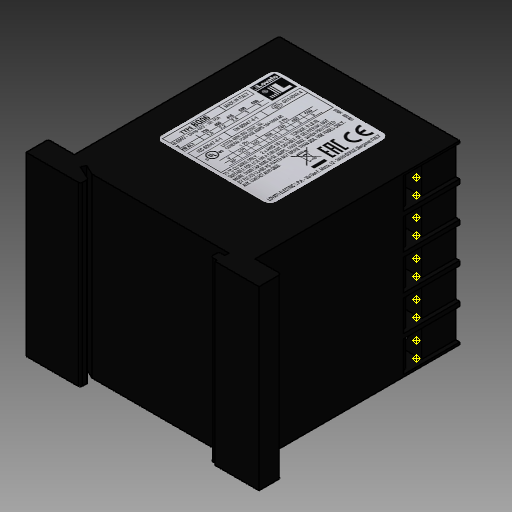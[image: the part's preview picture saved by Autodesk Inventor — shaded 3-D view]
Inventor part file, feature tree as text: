
AUTODESK INVENTOR PART (.ipt)
format: ipt  version: 2025.2 (Build 292293000, 293)  size: 1,169,408 bytes
history: native  units: mm
features: other x25, sketch x9, projected_geometry x9, extrude x7, fillet x1, mirror x1
ambient origin geometry x8: Origin, YZ Plane, XZ Plane, XY Plane, X Axis, Y Axis, Z Axis, Center Point
bodies: Solid1 (feature_tree)
feature tree (52):
  extrude  "Extrusion1"  Depth=6.5mm
  extrude  "Extrusion9"  Depth=5.5mm
  fillet  "Fillet2"  Radius=3.5mm
  extrude  "Extrusion10"  Depth=13.5mm
  extrude  "Extrusion11"  Depth=1.2mm
  extrude  "Extrusion13"  Depth=12.5mm
  extrude  "Extrusion14"  Depth=1.0mm
  other  "Decal1"
  other  "Decal2"
  other  "Sredina"
  sketch  "Sketch17"  dims[d18=44.0mm d19=0.0mm d20=0.5mm d21=55.5mm d93=6.0mm d99=40.0mm d101=8.5mm d102=10.0mm d104=10.0mm d107=8.0mm d108=5.0mm d109=6.0mm d110=5.0mm d111=7.0mm d112=9.0mm d113=3.0mm d114=7.5mm d115=1.0mm d116=0.0mm d117=0.5mm d118=14.0mm d119=7.7mm d120=0.95mm d121=50.0mm d123=8.6mm d124=10.0mm d126=10.0mm d128=0.95mm d129=1.0mm d130=0.0mm d131=4.0mm d132=8.5mm d133=50.0mm d135=8.6mm d136=10.0mm d138=10.0mm d140=10.0mm d141=0.0mm d142=10.0mm d143=8.8mm d145=10.0mm d147=50.0mm d148=1.05mm d149=14.0mm d150=7.7mm d152=0.0mm d153=1.0mm d154=4.0mm d155=8.5mm d156=50.0mm d158=8.8mm d159=10.0mm d161=10.0mm d163=10.0mm d164=0.0mm d165=10.0mm d166=0.0mm d172=44.0mm d173=45.0mm d186=30.0mm d199=3.85mm d200=7.7mm d201=3.0mm]
  other  "Work Point1"
  other  "Work Point2"
  other  "Work Point3"
  other  "Work Point4"
  other  "Work Point5"
  other  "Work Point6"
  other  "Work Point7"
  other  "Work Point8"
  other  "Work Point9"
  other  "Work Point10"
  mirror  "Mirror1"
  sketch  "Sketch9"  dims[d13=11.0mm d14=1.0mm]
  sketch  "Sketch Rectangular Pattern1"  dims[d0=58.0mm d1=6.5mm]
  sketch  "Sketch Rectangular Pattern2"  dims[d2=6.5mm d4=5.5mm d6=3.5mm]
  projected_geometry  "Projected Loop9"
  projected_geometry  "Projected Loop10"
  projected_geometry  "Projected Loop11"
  projected_geometry  "Projected Loop12"
  sketch  "Sketch Rectangular Pattern3"  dims[d7=13.5mm d8=1.9mm]
  sketch  "Sketch12"  dims[d15=0.5mm d16=3.5mm]
  sketch  "Sketch Rectangular Pattern4"  dims[d9=1.2mm d10=4.363323mm]
  projected_geometry  "Projected Loop13"
  projected_geometry  "Projected Loop14"
  projected_geometry  "Projected Loop15"
  projected_geometry  "Projected Loop16"
  sketch  "Sketch Rectangular Pattern5"  dims[d11=4.0mm d12=12.5mm]
  other  "Image1"
  sketch  "Sketch16"  dims[d17=0.5mm]
  other  "Image2"
  projected_geometry  "Projected Loop17"
  other  "Work Point11"
  other  "Work Point12"
  other  "Work Point13"
  other  "Work Point14"
  other  "Work Point15"
  other  "Work Point16"
  other  "Work Point17"
  other  "Work Point18"
  other  "Work Point19"
  other  "Work Point20"
  extrude  "Extrusion12"  Depth=3.5mm
